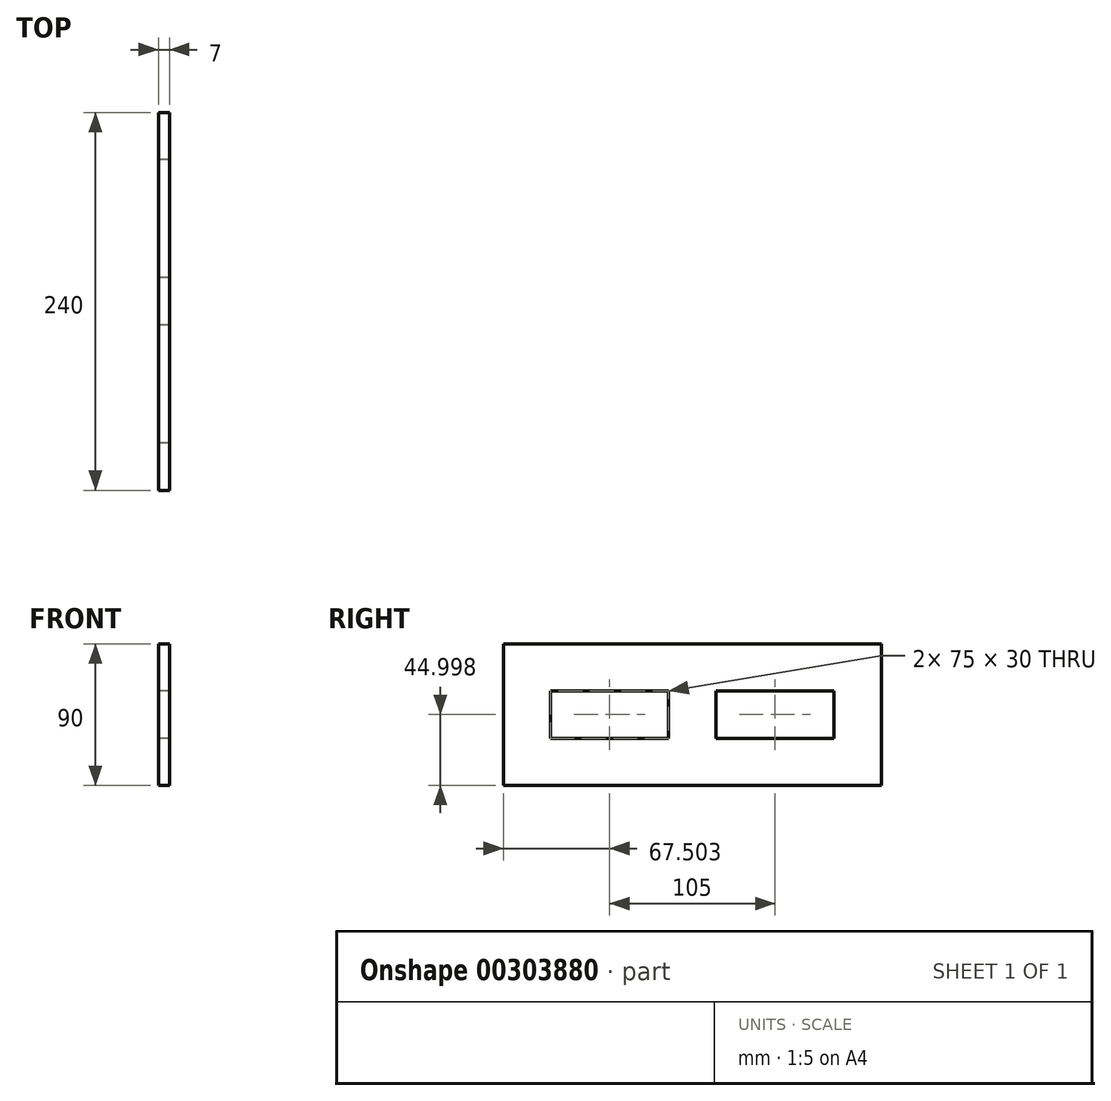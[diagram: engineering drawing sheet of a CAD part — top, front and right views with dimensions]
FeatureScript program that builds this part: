
annotation { "Feature Type Name" : "Feature", "Feature Type Description" : "" }
export const myFeature = defineFeature(function(context is Context, id is Id, definition is map)
    precondition{}
    {
        {
            var Q0;
            Q0=qCreatedBy(makeId("Right.planeOp"),FACE);
            var sketch = newSketch(context, id + "F0", { "sketchPlane" : qUnion([Q0])});
            skLineSegment(sketch, "E0.left", {"start": v(-196.92, 91.76) * mm, "end": v(-196.92, -58.24) * mm});
            skLineSegment(sketch, "E1.bottom", {"start": v(-196.92, 91.76) * mm, "end": v(169.76, 96.42) * mm});
            skLineSegment(sketch, "E1.top", {"start": v(-196.92, -58.24) * mm, "end": v(169.76, 6.42) * mm});
            skLineSegment(sketch, "E1.right", {"start": v(169.76, 96.42) * mm, "end": v(169.76, 6.42) * mm});
            skLineSegment(sketch, "E2.0", {"start": v(-166.92, 62.14) * mm, "end": v(-166.92, -22.49) * mm});
            skLineSegment(sketch, "E2.1", {"start": v(-166.92, 62.14) * mm, "end": v(-65.11, 63.43) * mm});
            skLineSegment(sketch, "E2.2", {"start": v(139.76, 66.03) * mm, "end": v(139.76, 31.6) * mm});
            skLineSegment(sketch, "E2.3", {"start": v(-166.92, -22.49) * mm, "end": v(-64.25, -4.38) * mm});
            skLineSegment(sketch, "E3", {"start": v(-65.11, 63.43) * mm, "end": v(-64.25, -4.38) * mm});
            skLineSegment(sketch, "E4", {"start": v(33.57, 64.69) * mm, "end": v(34.22, 12.98) * mm});
            skLineSegment(sketch, "E5.trimOffspring", {"start": v(33.57, 64.69) * mm, "end": v(139.76, 66.03) * mm});
            skLineSegment(sketch, "E6.trimOffspring", {"start": v(34.22, 12.98) * mm, "end": v(139.76, 31.6) * mm});
            skLineSegment(sketch, "E7.bottom", {"start": v(169.76, 96.42) * mm, "end": v(409.76, 96.42) * mm});
            skLineSegment(sketch, "E7.top", {"start": v(169.76, 6.42) * mm, "end": v(409.76, 6.42) * mm});
            skLineSegment(sketch, "E7.right", {"start": v(409.76, 96.42) * mm, "end": v(409.76, 6.42) * mm});
            skLineSegment(sketch, "E8.0", {"start": v(199.76, 66.42) * mm, "end": v(199.76, 36.42) * mm});
            skLineSegment(sketch, "E8.1", {"start": v(199.76, 66.42) * mm, "end": v(274.76, 66.42) * mm});
            skLineSegment(sketch, "E8.2", {"start": v(379.76, 66.42) * mm, "end": v(379.76, 36.42) * mm});
            skLineSegment(sketch, "E8.3", {"start": v(199.76, 36.42) * mm, "end": v(274.76, 36.42) * mm});
            skLineSegment(sketch, "E9", {"start": v(274.76, 66.42) * mm, "end": v(274.76, 36.42) * mm});
            skLineSegment(sketch, "E10", {"start": v(304.76, 66.42) * mm, "end": v(304.76, 36.42) * mm});
            skLineSegment(sketch, "E11.trimOffspring", {"start": v(304.76, 66.42) * mm, "end": v(379.76, 66.42) * mm});
            skLineSegment(sketch, "E12.trimOffspring", {"start": v(304.76, 36.42) * mm, "end": v(379.76, 36.42) * mm});
            skSolve(sketch);
        }
        {
            var Q0;
            Q0=makeQuery(id+"F0.imprint","IMPRINT",FACE,{"disambiguationData":[TD([[makeQuery(id+"F0.imprint","IMPRINT",EDGE,{"derivedFrom":sQuery(id+"F0.wireOp",EDGE,"E7.bottom")}),-1.0]])]});
            extrude(context, id + "F1", {"entities" : qUnion([Q0]), "depth" : 7 * mm});
        }
    });
